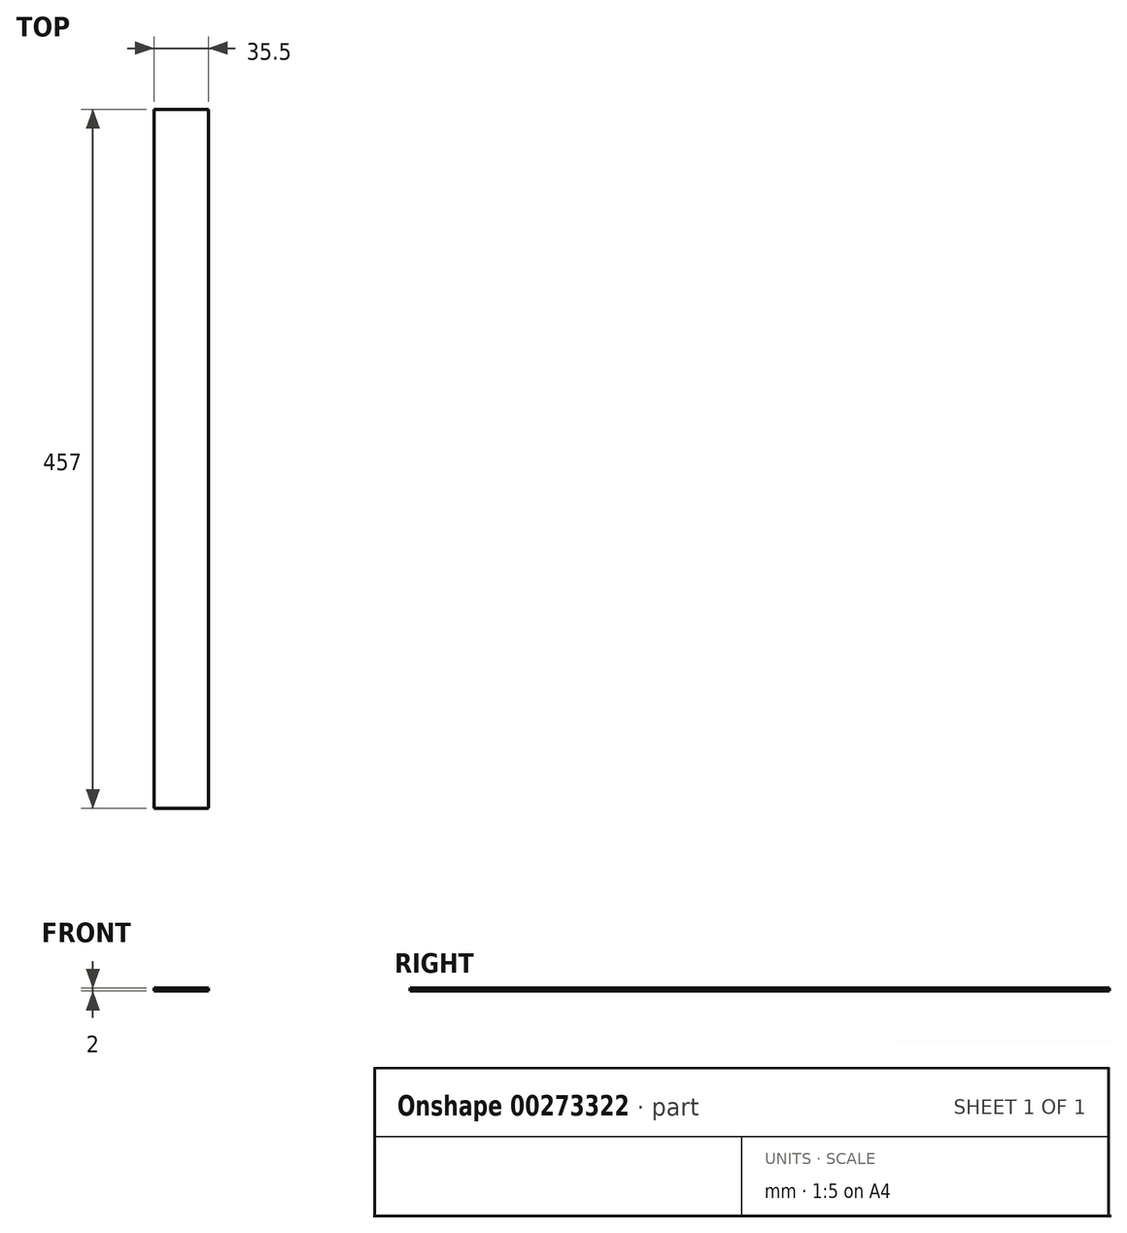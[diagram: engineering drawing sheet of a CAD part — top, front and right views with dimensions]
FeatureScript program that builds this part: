
annotation { "Feature Type Name" : "Feature", "Feature Type Description" : "" }
export const myFeature = defineFeature(function(context is Context, id is Id, definition is map)
    precondition{}
    {
        {
            var Q0;
            Q0=qCreatedBy(makeId("Top.planeOp"),FACE);
            var sketch = newSketch(context, id + "F0", { "sketchPlane" : qUnion([Q0])});
            skLineSegment(sketch, "E0.bottom", {"start": v(-22.74, 250.2) * mm, "end": v(12.76, 250.2) * mm});
            skLineSegment(sketch, "E0.top", {"start": v(-22.74, -206.8) * mm, "end": v(12.76, -206.8) * mm});
            skLineSegment(sketch, "E0.left", {"start": v(-22.74, 250.2) * mm, "end": v(-22.74, -206.8) * mm});
            skLineSegment(sketch, "E0.right", {"start": v(12.76, 250.2) * mm, "end": v(12.76, -206.8) * mm});
            skSolve(sketch);
        }
        {
            var Q0;
            Q0=makeQuery(id+"F0.imprint","IMPRINT",FACE,{"disambiguationData":[TD([[makeQuery(id+"F0.imprint","IMPRINT",EDGE,{"derivedFrom":sQuery(id+"F0.wireOp",EDGE,"E0.bottom")}),-1.0]])]});
            extrude(context, id + "F1", {"entities" : qUnion([Q0]), "depth" : 2 * mm});
        }
    });
